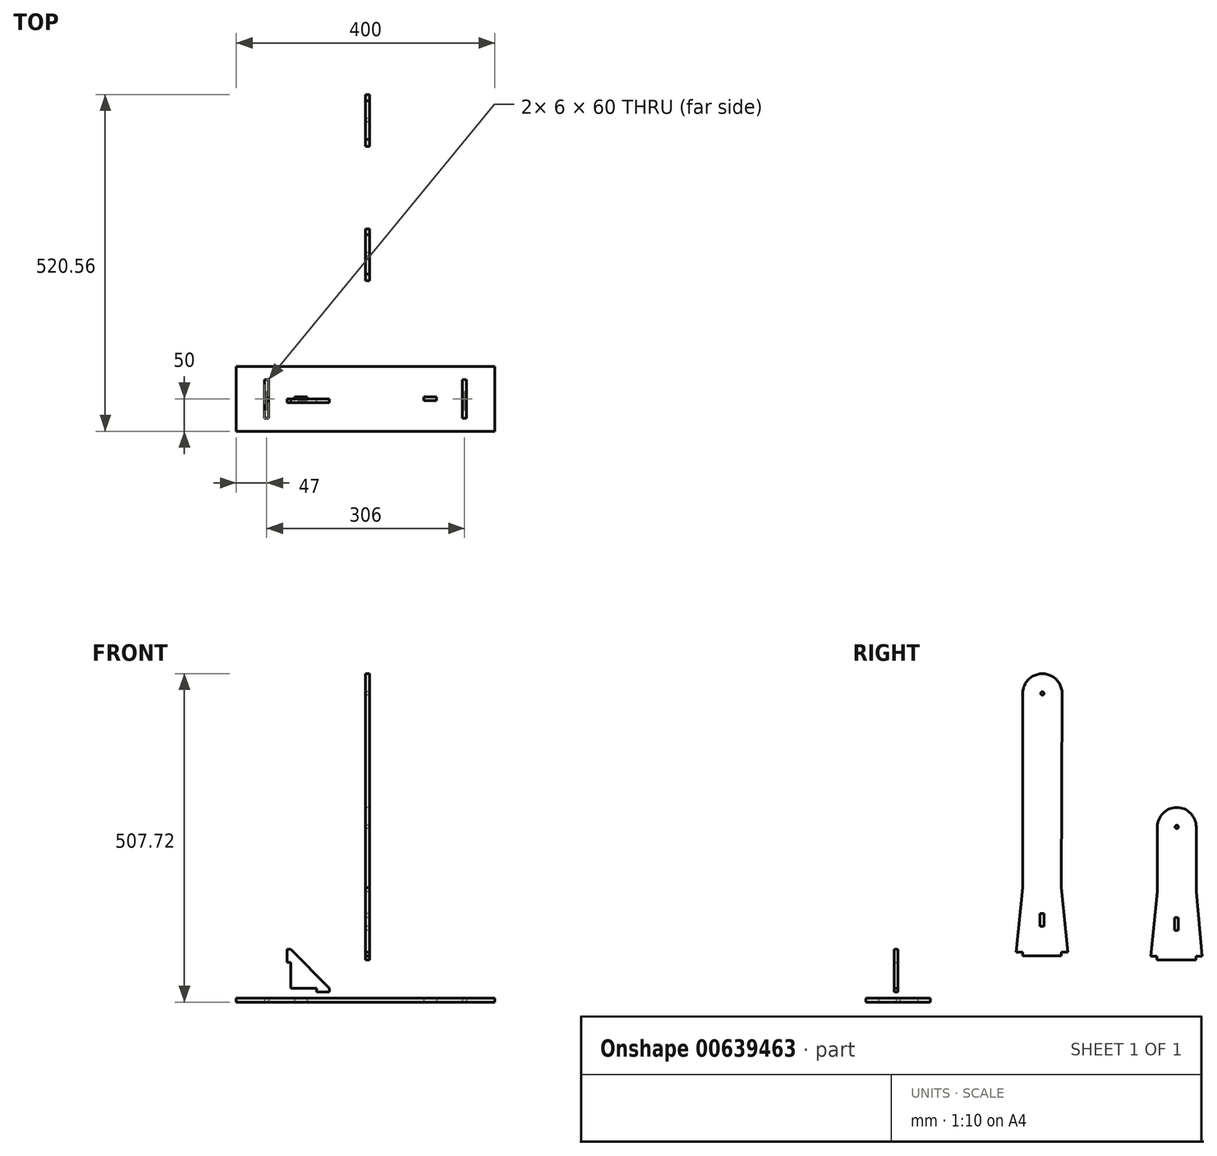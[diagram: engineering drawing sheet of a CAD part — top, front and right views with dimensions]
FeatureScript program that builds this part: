
annotation { "Feature Type Name" : "Feature", "Feature Type Description" : "" }
export const myFeature = defineFeature(function(context is Context, id is Id, definition is map)
    precondition{}
    {
        {
            var Q0;
            Q0=qCreatedBy(makeId("Top.planeOp"),FACE);
            var sketch = newSketch(context, id + "F0", { "sketchPlane" : qUnion([Q0])});
            skLineSegment(sketch, "E0.bottom", {"start": v(200, -50) * mm, "end": v(-200, -50) * mm});
            skLineSegment(sketch, "E0.top", {"start": v(200, 50) * mm, "end": v(-200, 50) * mm});
            skLineSegment(sketch, "E0.left", {"start": v(200, -50) * mm, "end": v(200, 50) * mm});
            skLineSegment(sketch, "E0.right", {"start": v(-200, -50) * mm, "end": v(-200, 50) * mm});
            skPoint(sketch, "E0.middle", {"position": v(0, 0) * mm});
            skLineSegment(sketch, "E1.bottom", {"start": v(-150, -30) * mm, "end": v(-156, -30) * mm});
            skLineSegment(sketch, "E1.top", {"start": v(-150, 30) * mm, "end": v(-156, 30) * mm});
            skLineSegment(sketch, "E1.left", {"start": v(-150, -30) * mm, "end": v(-150, 30) * mm});
            skLineSegment(sketch, "E1.right", {"start": v(-156, -30) * mm, "end": v(-156, 30) * mm});
            skPoint(sketch, "E1.middle", {"position": v(-153, 0) * mm});
            skLineSegment(sketch, "E2.bottom", {"start": v(-90, -3) * mm, "end": v(-110, -3) * mm});
            skLineSegment(sketch, "E2.top", {"start": v(-90, 3) * mm, "end": v(-110, 3) * mm});
            skLineSegment(sketch, "E2.left", {"start": v(-90, -3) * mm, "end": v(-90, 3) * mm});
            skLineSegment(sketch, "E2.right", {"start": v(-110, -3) * mm, "end": v(-110, 3) * mm});
            skPoint(sketch, "E2.middle", {"position": v(-100, 0) * mm});
            skPoint(sketch, "E3.MirrorP", {"position": v(100, 0) * mm});
            skLineSegment(sketch, "E4.MirrorCS", {"start": v(90, -3) * mm, "end": v(110, -3) * mm});
            skLineSegment(sketch, "E5.MirrorCS", {"start": v(110, -3) * mm, "end": v(110, 3) * mm});
            skLineSegment(sketch, "E6.MirrorCS", {"start": v(90, 3) * mm, "end": v(110, 3) * mm});
            skLineSegment(sketch, "E7.MirrorCS", {"start": v(90, -3) * mm, "end": v(90, 3) * mm});
            skLineSegment(sketch, "E8.MirrorCS", {"start": v(150, -30) * mm, "end": v(150, 30) * mm});
            skPoint(sketch, "E9.MirrorP", {"position": v(153, 0) * mm});
            skLineSegment(sketch, "E10.MirrorCS", {"start": v(156, -30) * mm, "end": v(156, 30) * mm});
            skLineSegment(sketch, "E11.MirrorCS", {"start": v(150, 30) * mm, "end": v(156, 30) * mm});
            skLineSegment(sketch, "E12.MirrorCS", {"start": v(150, -30) * mm, "end": v(156, -30) * mm});
            skSolve(sketch);
        }
        {
            var Q0;
            Q0=makeQuery(id+"F0.imprint","IMPRINT",FACE,{"disambiguationData":[TD([[makeQuery(id+"F0.imprint","IMPRINT",EDGE,{"derivedFrom":sQuery(id+"F0.wireOp",EDGE,"E0.bottom")}),-1.0]])]});
            extrude(context, id + "F1", {"entities" : qUnion([Q0]), "depth" : 6 * mm, "offsetDistance" : 25 * mm});
        }
        {
            var Q0;
            Q0=qCreatedBy(makeId("Front.planeOp"),FACE);
            var sketch = newSketch(context, id + "F2", { "sketchPlane" : qUnion([Q0])});
            skLineSegment(sketch, "E13", {"start": v(-115.66, 81.51) * mm, "end": v(-55.66, 21.51) * mm});
            skLineSegment(sketch, "E14", {"start": v(-55.66, 21.51) * mm, "end": v(-55.66, 15.51) * mm});
            skLineSegment(sketch, "E15", {"start": v(-55.66, 15.51) * mm, "end": v(-75.66, 15.51) * mm});
            skLineSegment(sketch, "E16", {"start": v(-75.66, 15.51) * mm, "end": v(-75.66, 21.51) * mm});
            skLineSegment(sketch, "E17", {"start": v(-115.66, 81.51) * mm, "end": v(-121.66, 81.51) * mm});
            skLineSegment(sketch, "E18", {"start": v(-121.66, 81.51) * mm, "end": v(-121.66, 61.51) * mm});
            skLineSegment(sketch, "E19", {"start": v(-121.66, 61.51) * mm, "end": v(-115.66, 61.51) * mm});
            skLineSegment(sketch, "E20", {"start": v(-115.66, 61.51) * mm, "end": v(-115.66, 21.51) * mm});
            skLineSegment(sketch, "E21", {"start": v(-115.66, 21.51) * mm, "end": v(-75.66, 21.51) * mm});
            skSolve(sketch);
        }
        {
            var Q0;
            Q0 = qSketchRegion(id + "F2", true);
            extrude(context, id + "F3", {"entities" : qUnion([Q0]), "depth" : 6 * mm, "offsetDistance" : 25 * mm});
        }
        {
            var Q0;
            Q0=qCreatedBy(makeId("Right.planeOp"),FACE);
            var sketch = newSketch(context, id + "F4", { "sketchPlane" : qUnion([Q0])});
            skLineSegment(sketch, "E22.bottom", {"start": v(253.69, 477.12) * mm, "end": v(192.69, 477.22) * mm});
            skLineSegment(sketch, "E23", {"start": v(252.69, 77.22) * mm, "end": v(262.69, 77.22) * mm});
            skLineSegment(sketch, "E24", {"start": v(262.69, 77.22) * mm, "end": v(252.69, 176.72) * mm});
            skLineSegment(sketch, "E25", {"start": v(252.69, 77.22) * mm, "end": v(252.69, 71.22) * mm});
            skLineSegment(sketch, "E26.MirrorCS", {"start": v(182.69, 77.22) * mm, "end": v(192.69, 176.72) * mm});
            skLineSegment(sketch, "E27.MirrorCS", {"start": v(192.69, 77.22) * mm, "end": v(192.69, 71.22) * mm});
            skLineSegment(sketch, "E28", {"start": v(192.69, 71.22) * mm, "end": v(252.69, 71.22) * mm});
            skLineSegment(sketch, "E29", {"start": v(192.69, 477.22) * mm, "end": v(192.69, 176.72) * mm});
            skLineSegment(sketch, "E30", {"start": v(253.69, 477.12) * mm, "end": v(252.69, 176.72) * mm});
            skLineSegment(sketch, "E31", {"start": v(182.69, 77.22) * mm, "end": v(192.69, 77.22) * mm});
            skLineSegment(sketch, "E32.bottom", {"start": v(225.69, 117.22) * mm, "end": v(219.69, 117.22) * mm});
            skLineSegment(sketch, "E32.top", {"start": v(225.69, 137.22) * mm, "end": v(219.69, 137.22) * mm});
            skLineSegment(sketch, "E32.left", {"start": v(225.69, 117.22) * mm, "end": v(225.69, 137.22) * mm});
            skLineSegment(sketch, "E32.right", {"start": v(219.69, 117.22) * mm, "end": v(219.69, 137.22) * mm});
            skPoint(sketch, "E32.middle", {"position": v(222.69, 127.22) * mm});
            skPoint(sketch, "E32.middle.positionSnap0", {"position": v(222.69, 71.22) * mm});
            skPoint(sketch, "E32.centerSnap0", {"position": v(222.69, 71.22) * mm});
            skLineSegment(sketch, "E33", {"start": v(460.56, 70.87) * mm, "end": v(470.56, 70.87) * mm});
            skLineSegment(sketch, "E34", {"start": v(470.56, 70.87) * mm, "end": v(461.06, 170.42) * mm});
            skLineSegment(sketch, "E35", {"start": v(460.56, 70.87) * mm, "end": v(460.56, 64.87) * mm});
            skLineSegment(sketch, "E36.MirrorCS", {"start": v(390.56, 70.87) * mm, "end": v(401.06, 170.37) * mm});
            skLineSegment(sketch, "E37.MirrorCS", {"start": v(400.56, 70.87) * mm, "end": v(400.56, 64.87) * mm});
            skLineSegment(sketch, "E38", {"start": v(400.56, 64.87) * mm, "end": v(460.56, 64.87) * mm});
            skLineSegment(sketch, "E39", {"start": v(390.56, 70.87) * mm, "end": v(400.56, 70.87) * mm});
            skLineSegment(sketch, "E40.bottom", {"start": v(433.56, 110.87) * mm, "end": v(427.56, 110.87) * mm});
            skLineSegment(sketch, "E40.top", {"start": v(433.56, 130.87) * mm, "end": v(427.56, 130.87) * mm});
            skLineSegment(sketch, "E40.left", {"start": v(433.56, 110.87) * mm, "end": v(433.56, 130.87) * mm});
            skLineSegment(sketch, "E40.right", {"start": v(427.56, 110.87) * mm, "end": v(427.56, 130.87) * mm});
            skPoint(sketch, "E40.middle", {"position": v(430.56, 120.87) * mm});
            skPoint(sketch, "E40.middle.positionSnap0", {"position": v(430.56, 64.87) * mm});
            skPoint(sketch, "E40.centerSnap0", {"position": v(430.56, 64.87) * mm});
            skLineSegment(sketch, "E41", {"start": v(401.06, 170.37) * mm, "end": v(401.06, 270.87) * mm});
            skLineSegment(sketch, "E42", {"start": v(461.06, 170.42) * mm, "end": v(461.06, 270.87) * mm});
            skLineSegment(sketch, "E43", {"start": v(461.06, 270.87) * mm, "end": v(401.06, 270.87) * mm});
            skArc(sketch, "E44", {"start": v(461.06, 270.87) * mm, "mid": v(431.06, 300.87) * mm, "end": v(401.06, 270.87) * mm});
            skArc(sketch, "E45", {"start": v(253.69, 477.12) * mm, "mid": v(223.24, 507.72) * mm, "end": v(192.69, 477.22) * mm});
            skCircle(sketch, "E46", {"center": v(431.06, 270.87) * mm, "radius": 2.5 * mm});
            skCircle(sketch, "E47", {"center": v(223.19, 477.22) * mm, "radius": 2.5 * mm});
            skSolve(sketch);
        }
        {
            var Q0;
            {var subQ0=sQuery(id+"F4.wireOp",EDGE,"E45");Q0=makeQuery(id+"F4.imprint","IMPRINT",FACE,{"disambiguationData":[TD([[makeQuery(id+"F4.imprint","IMPRINT",EDGE,{"derivedFrom":subQ0}),1.0]])]});}
            var Q1;
            Q1=makeQuery(id+"F4.imprint","IMPRINT",FACE,{"disambiguationData":[TD([[makeQuery(id+"F4.imprint","IMPRINT",EDGE,{"derivedFrom":sQuery(id+"F4.wireOp",EDGE,"E23")}),1.0]])]});
            extrude(context, id + "F5", {"entities" : qUnion([Q0, Q1]), "depth" : 6 * mm, "offsetDistance" : 25 * mm});
        }
        {
            var Q0;
            Q0 = qSketchRegion(id + "F4", true);
            extrude(context, id + "F6", {"entities" : qUnion([Q0]), "depth" : 6 * mm, "offsetDistance" : 25 * mm});
        }
    });
